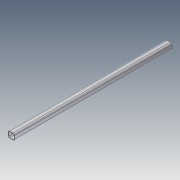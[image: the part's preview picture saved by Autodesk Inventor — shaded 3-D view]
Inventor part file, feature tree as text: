
AUTODESK INVENTOR PART (.ipt)
format: ipt  version: unknown  size: 198,144 bytes
history: native  units: in
note: dims shown in document units (in); Inventor stores cm internally (conversion verified against a paired STEP export)
features: extrude x2, sketch x2
ambient origin geometry x8: Origin, YZ Plane, XZ Plane, XY Plane, X Axis, Y Axis, Z Axis, Center Point
bodies: Solid1 (feature_tree)
feature tree (4):
  extrude  "Extrusion1"  Depth=0.375in
  extrude  "Extrusion2"  Depth=37.125in TaperAngle=0.0deg
  sketch  "Sketch1"  dims[d0=1.5in d1=0.375in]
  sketch  "Sketch2"  dims[d2=0.125in d3=37.125in d4=0.0in d5=0.0206in d6=0.0206in d7=37.0in d8=0.0in]
